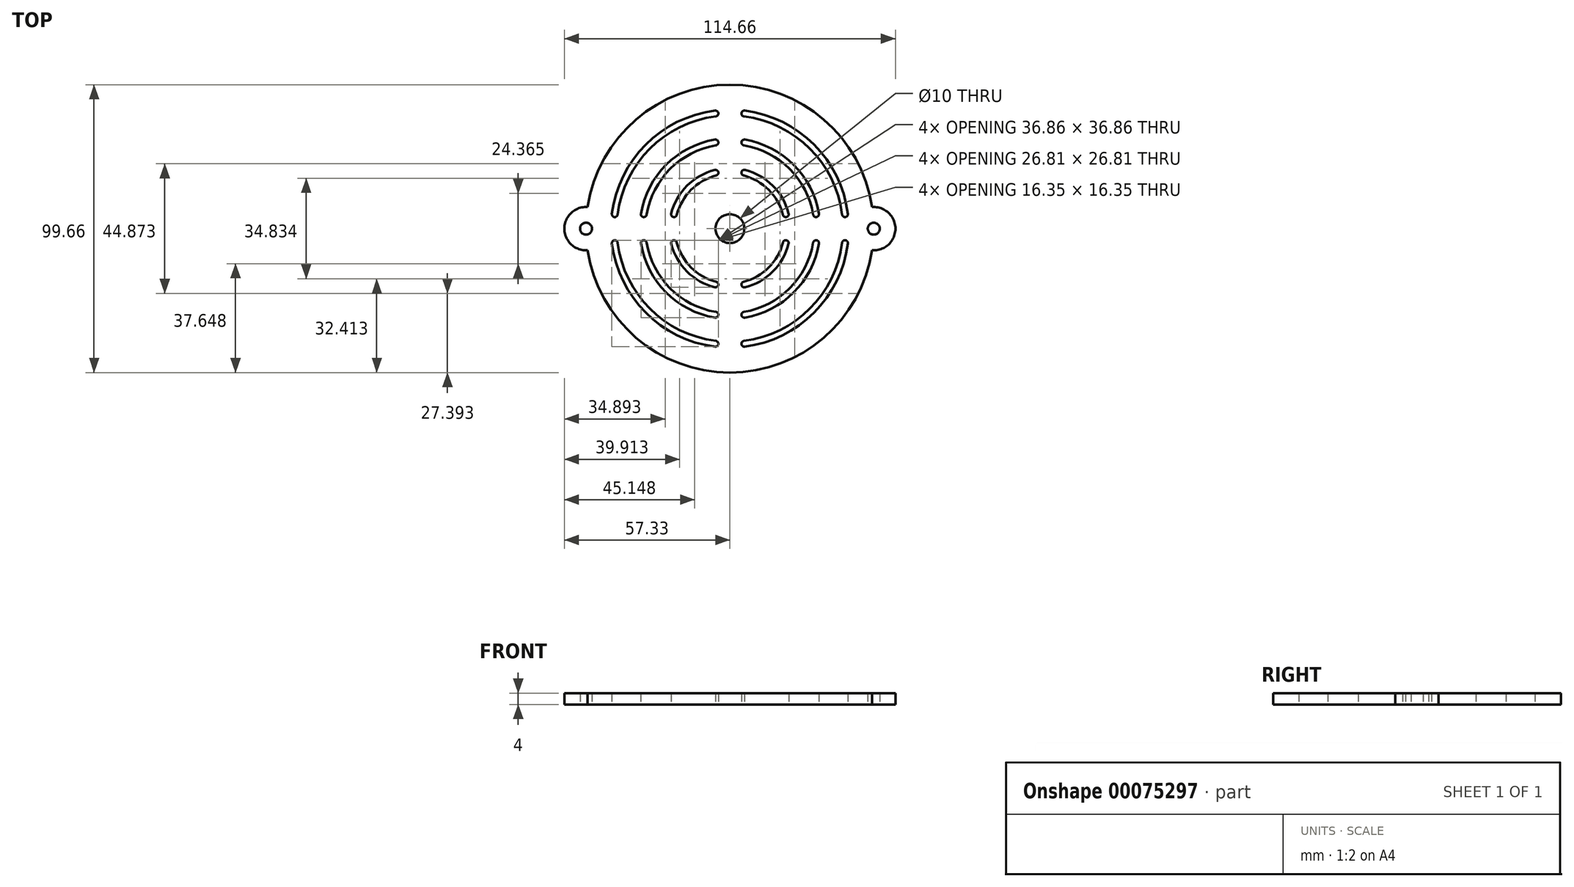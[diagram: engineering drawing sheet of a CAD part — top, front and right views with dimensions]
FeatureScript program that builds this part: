
annotation { "Feature Type Name" : "Feature", "Feature Type Description" : "" }
export const myFeature = defineFeature(function(context is Context, id is Id, definition is map)
    precondition{}
    {
        {
            var Q0;
            Q0=qCreatedBy(makeId("Top.planeOp"),FACE);
            var sketch = newSketch(context, id + "F0", { "sketchPlane" : qUnion([Q0])});
            skCircle(sketch, "E0", {"center": v(-49.83, 0) * mm, "radius": 2.08 * mm});
            skCircle(sketch, "E1", {"center": v(49.83, 0) * mm, "radius": 2.08 * mm});
            skLineSegment(sketch, "E2", {"start": v(0, 50.77) * mm, "end": v(0, -49.23) * mm, "construction": true});
            skArc(sketch, "E3", {"start": v(-49.27, 7.48) * mm, "mid": v(-57.33, 0) * mm, "end": v(-49.27, -7.48) * mm});
            skArc(sketch, "E4", {"start": v(49.27, -7.48) * mm, "mid": v(57.33, 0) * mm, "end": v(49.27, 7.48) * mm});
            skArc(sketch, "E5.trimOffspring", {"start": v(-49.27, -7.48) * mm, "mid": v(0, -49.83) * mm, "end": v(49.27, -7.48) * mm});
            skArc(sketch, "E6.trimOffspring", {"start": v(49.27, 7.48) * mm, "mid": v(0, 49.83) * mm, "end": v(-49.27, 7.48) * mm});
            skCircle(sketch, "E7", {"center": v(0, 0) * mm, "radius": 5 * mm});
            skArc(sketch, "E8.0.startCap", {"start": v(-5.12, 40.87) * mm, "mid": v(-4, 40) * mm, "end": v(-4.88, 38.88) * mm});
            skArc(sketch, "E8.0.endCap", {"start": v(-38.88, 4.88) * mm, "mid": v(-40, 4) * mm, "end": v(-40.87, 5.12) * mm});
            skArc(sketch, "E8.0.left", {"start": v(-4.88, 38.88) * mm, "mid": v(-27.7, 27.7) * mm, "end": v(-38.88, 4.88) * mm});
            skArc(sketch, "E8.0.right", {"start": v(-5.12, 40.87) * mm, "mid": v(-29.12, 29.12) * mm, "end": v(-40.87, 5.12) * mm});
            skArc(sketch, "E8.1.startCap", {"start": v(-5.17, 30.82) * mm, "mid": v(-4.01, 30) * mm, "end": v(-4.83, 28.85) * mm});
            skArc(sketch, "E8.1.endCap", {"start": v(-28.85, 4.83) * mm, "mid": v(-30, 4.01) * mm, "end": v(-30.82, 5.17) * mm});
            skArc(sketch, "E8.1.left", {"start": v(-4.83, 28.85) * mm, "mid": v(-20.68, 20.68) * mm, "end": v(-28.85, 4.83) * mm});
            skArc(sketch, "E8.1.right", {"start": v(-5.17, 30.82) * mm, "mid": v(-22.1, 22.1) * mm, "end": v(-30.82, 5.17) * mm});
            skArc(sketch, "E8.2.startCap", {"start": v(-5.25, 20.33) * mm, "mid": v(-4.03, 19.61) * mm, "end": v(-4.75, 18.4) * mm});
            skArc(sketch, "E8.2.endCap", {"start": v(-18.4, 4.75) * mm, "mid": v(-19.61, 4.03) * mm, "end": v(-20.33, 5.25) * mm});
            skArc(sketch, "E8.2.left", {"start": v(-4.75, 18.4) * mm, "mid": v(-13.44, 13.44) * mm, "end": v(-18.4, 4.75) * mm});
            skArc(sketch, "E8.2.right", {"start": v(-5.25, 20.33) * mm, "mid": v(-14.85, 14.85) * mm, "end": v(-20.33, 5.25) * mm});
            skArc(sketch, "E9.1.0", {"start": v(-40.87, -5.12) * mm, "mid": v(-29.12, -29.12) * mm, "end": v(-5.12, -40.87) * mm});
            skArc(sketch, "E9.1.1", {"start": v(-18.4, -4.75) * mm, "mid": v(-13.44, -13.44) * mm, "end": v(-4.75, -18.4) * mm});
            skArc(sketch, "E9.1.2", {"start": v(-38.88, -4.88) * mm, "mid": v(-27.7, -27.7) * mm, "end": v(-4.88, -38.88) * mm});
            skArc(sketch, "E9.1.3", {"start": v(-30.82, -5.17) * mm, "mid": v(-22.1, -22.1) * mm, "end": v(-5.17, -30.82) * mm});
            skArc(sketch, "E9.1.4", {"start": v(-28.85, -4.83) * mm, "mid": v(-20.68, -20.68) * mm, "end": v(-4.83, -28.85) * mm});
            skArc(sketch, "E9.1.5", {"start": v(-20.33, -5.25) * mm, "mid": v(-14.85, -14.85) * mm, "end": v(-5.25, -20.33) * mm});
            skArc(sketch, "E9.1.6", {"start": v(-20.33, -5.25) * mm, "mid": v(-19.61, -4.03) * mm, "end": v(-18.4, -4.75) * mm});
            skArc(sketch, "E9.1.7", {"start": v(-4.88, -38.88) * mm, "mid": v(-4, -40) * mm, "end": v(-5.12, -40.87) * mm});
            skArc(sketch, "E9.1.8", {"start": v(-30.82, -5.17) * mm, "mid": v(-30, -4.01) * mm, "end": v(-28.85, -4.83) * mm});
            skArc(sketch, "E9.1.9", {"start": v(-40.87, -5.12) * mm, "mid": v(-40, -4) * mm, "end": v(-38.88, -4.88) * mm});
            skArc(sketch, "E9.1.10", {"start": v(-4.75, -18.4) * mm, "mid": v(-4.03, -19.61) * mm, "end": v(-5.25, -20.33) * mm});
            skArc(sketch, "E9.1.11", {"start": v(-4.83, -28.85) * mm, "mid": v(-4.01, -30) * mm, "end": v(-5.17, -30.82) * mm});
            skArc(sketch, "E9.2.0", {"start": v(5.12, -40.87) * mm, "mid": v(29.12, -29.12) * mm, "end": v(40.87, -5.12) * mm});
            skArc(sketch, "E9.2.1", {"start": v(4.75, -18.4) * mm, "mid": v(13.44, -13.44) * mm, "end": v(18.4, -4.75) * mm});
            skArc(sketch, "E9.2.2", {"start": v(4.88, -38.88) * mm, "mid": v(27.7, -27.7) * mm, "end": v(38.88, -4.88) * mm});
            skArc(sketch, "E9.2.3", {"start": v(5.17, -30.82) * mm, "mid": v(22.1, -22.1) * mm, "end": v(30.82, -5.17) * mm});
            skArc(sketch, "E9.2.4", {"start": v(4.83, -28.85) * mm, "mid": v(20.68, -20.68) * mm, "end": v(28.85, -4.83) * mm});
            skArc(sketch, "E9.2.5", {"start": v(5.25, -20.33) * mm, "mid": v(14.85, -14.85) * mm, "end": v(20.33, -5.25) * mm});
            skArc(sketch, "E9.2.6", {"start": v(5.25, -20.33) * mm, "mid": v(4.03, -19.61) * mm, "end": v(4.75, -18.4) * mm});
            skArc(sketch, "E9.2.7", {"start": v(38.88, -4.88) * mm, "mid": v(40, -4) * mm, "end": v(40.87, -5.12) * mm});
            skArc(sketch, "E9.2.8", {"start": v(5.17, -30.82) * mm, "mid": v(4.01, -30) * mm, "end": v(4.83, -28.85) * mm});
            skArc(sketch, "E9.2.9", {"start": v(5.12, -40.87) * mm, "mid": v(4, -40) * mm, "end": v(4.88, -38.88) * mm});
            skArc(sketch, "E9.2.10", {"start": v(18.4, -4.75) * mm, "mid": v(19.61, -4.03) * mm, "end": v(20.33, -5.25) * mm});
            skArc(sketch, "E9.2.11", {"start": v(28.85, -4.83) * mm, "mid": v(30, -4.01) * mm, "end": v(30.82, -5.17) * mm});
            skArc(sketch, "E9.3.0", {"start": v(40.87, 5.12) * mm, "mid": v(29.12, 29.12) * mm, "end": v(5.12, 40.87) * mm});
            skArc(sketch, "E9.3.1", {"start": v(18.4, 4.75) * mm, "mid": v(13.44, 13.44) * mm, "end": v(4.75, 18.4) * mm});
            skArc(sketch, "E9.3.2", {"start": v(38.88, 4.88) * mm, "mid": v(27.7, 27.7) * mm, "end": v(4.88, 38.88) * mm});
            skArc(sketch, "E9.3.3", {"start": v(30.82, 5.17) * mm, "mid": v(22.1, 22.1) * mm, "end": v(5.17, 30.82) * mm});
            skArc(sketch, "E9.3.4", {"start": v(28.85, 4.83) * mm, "mid": v(20.68, 20.68) * mm, "end": v(4.83, 28.85) * mm});
            skArc(sketch, "E9.3.5", {"start": v(20.33, 5.25) * mm, "mid": v(14.85, 14.85) * mm, "end": v(5.25, 20.33) * mm});
            skArc(sketch, "E9.3.6", {"start": v(20.33, 5.25) * mm, "mid": v(19.61, 4.03) * mm, "end": v(18.4, 4.75) * mm});
            skArc(sketch, "E9.3.7", {"start": v(4.88, 38.88) * mm, "mid": v(4, 40) * mm, "end": v(5.12, 40.87) * mm});
            skArc(sketch, "E9.3.8", {"start": v(30.82, 5.17) * mm, "mid": v(30, 4.01) * mm, "end": v(28.85, 4.83) * mm});
            skArc(sketch, "E9.3.9", {"start": v(40.87, 5.12) * mm, "mid": v(40, 4) * mm, "end": v(38.88, 4.88) * mm});
            skArc(sketch, "E9.3.10", {"start": v(4.75, 18.4) * mm, "mid": v(4.03, 19.61) * mm, "end": v(5.25, 20.33) * mm});
            skArc(sketch, "E9.3.11", {"start": v(4.83, 28.85) * mm, "mid": v(4.01, 30) * mm, "end": v(5.17, 30.82) * mm});
            skSolve(sketch);
        }
        {
            var Q0;
            Q0 = qSketchRegion(id + "F0", true);
            extrude(context, id + "F1", {"entities" : qUnion([Q0]), "depth" : 4 * mm});
        }
    });
